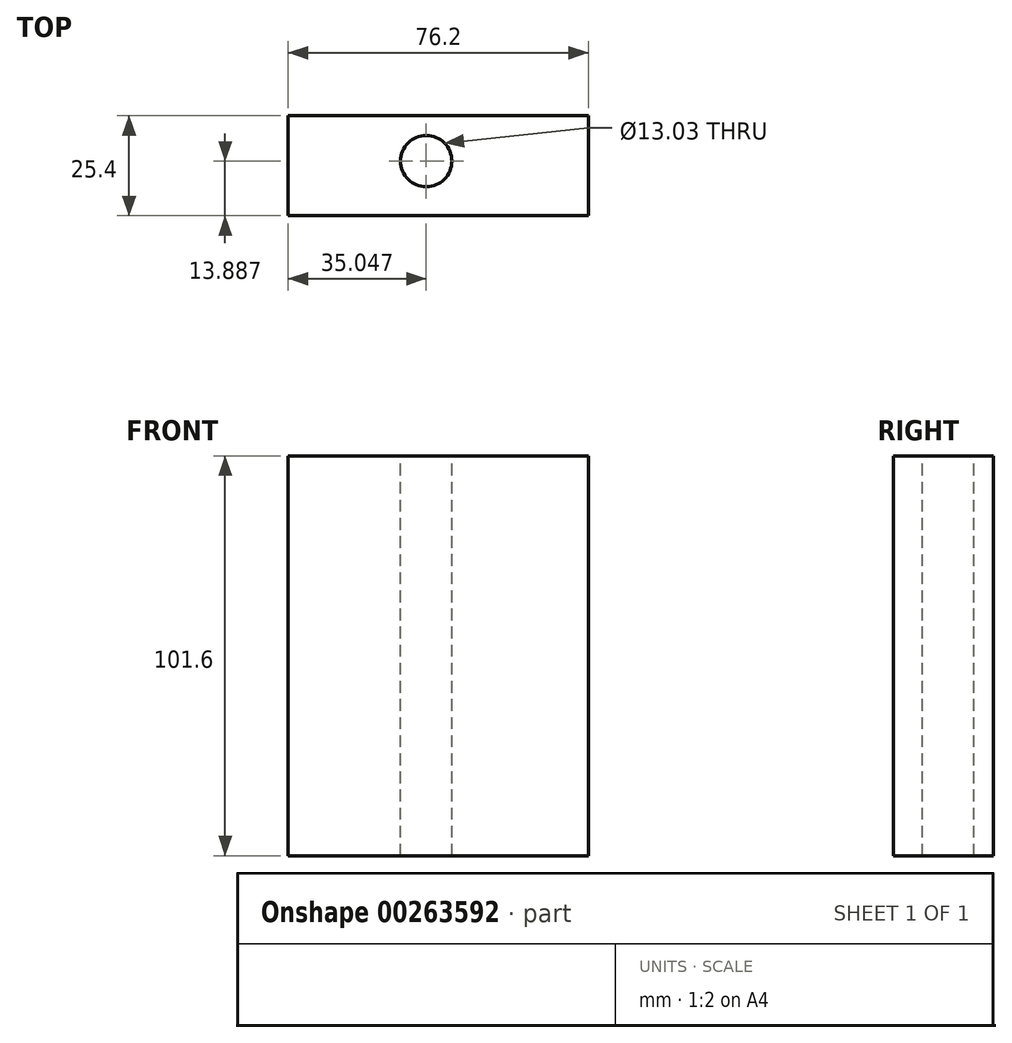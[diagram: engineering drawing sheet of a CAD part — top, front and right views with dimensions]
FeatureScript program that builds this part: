
annotation { "Feature Type Name" : "Feature", "Feature Type Description" : "" }
export const myFeature = defineFeature(function(context is Context, id is Id, definition is map)
    precondition{}
    {
        {
            var Q0;
            Q0=qCreatedBy(makeId("Front.planeOp"),FACE);
            var sketch = newSketch(context, id + "F0", { "sketchPlane" : qUnion([Q0])});
            skLineSegment(sketch, "E0.bottom", {"start": v(0, 0) * mm, "end": v(76.2, 0) * mm});
            skLineSegment(sketch, "E0.top", {"start": v(0, 101.6) * mm, "end": v(76.2, 101.6) * mm});
            skLineSegment(sketch, "E0.left", {"start": v(0, 0) * mm, "end": v(0, 101.6) * mm});
            skLineSegment(sketch, "E0.right", {"start": v(76.2, 0) * mm, "end": v(76.2, 101.6) * mm});
            skSolve(sketch);
        }
        {
            var Q0;
            Q0=makeQuery(id+"F0.imprint","IMPRINT",FACE,{"disambiguationData":[TD([[makeQuery(id+"F0.imprint","IMPRINT",EDGE,{"derivedFrom":sQuery(id+"F0.wireOp",EDGE,"E0.bottom")}),1.0]])]});
            extrude(context, id + "F1", {"entities" : qUnion([Q0]), "oppositeDirection" : true, "depth" : 25.4 * mm});
        }
        {
            var Q0;
            Q0=makeQuery(id+"F1.opExtrude","SWEPT_FACE",FACE,{"disambiguationData":[OSD([sQuery(id+"F0.wireOp",EDGE,"E0.top")])]});
            var sketch = newSketch(context, id + "F2", { "sketchPlane" : qUnion([Q0])});
            skCircle(sketch, "E1", {"center": v(35.05, 13.89) * mm, "radius": 6.52 * mm});
            skSolve(sketch);
        }
        {
            var Q0;
            Q0=makeQuery(id+"F2.imprint","IMPRINT",FACE,{"disambiguationData":[TD([[makeQuery(id+"F2.imprint","IMPRINT",EDGE,{"derivedFrom":sQuery(id+"F2.wireOp",EDGE,"E1")}),1.0]])]});
            extrude(context, id + "F3", {"entities" : qUnion([Q0]), "operationType" : NewBodyOperationType.REMOVE, "endBound" : BoundingType.UP_TO_NEXT, "oppositeDirection" : true, "depth" : 25.4 * mm});
        }
    });
